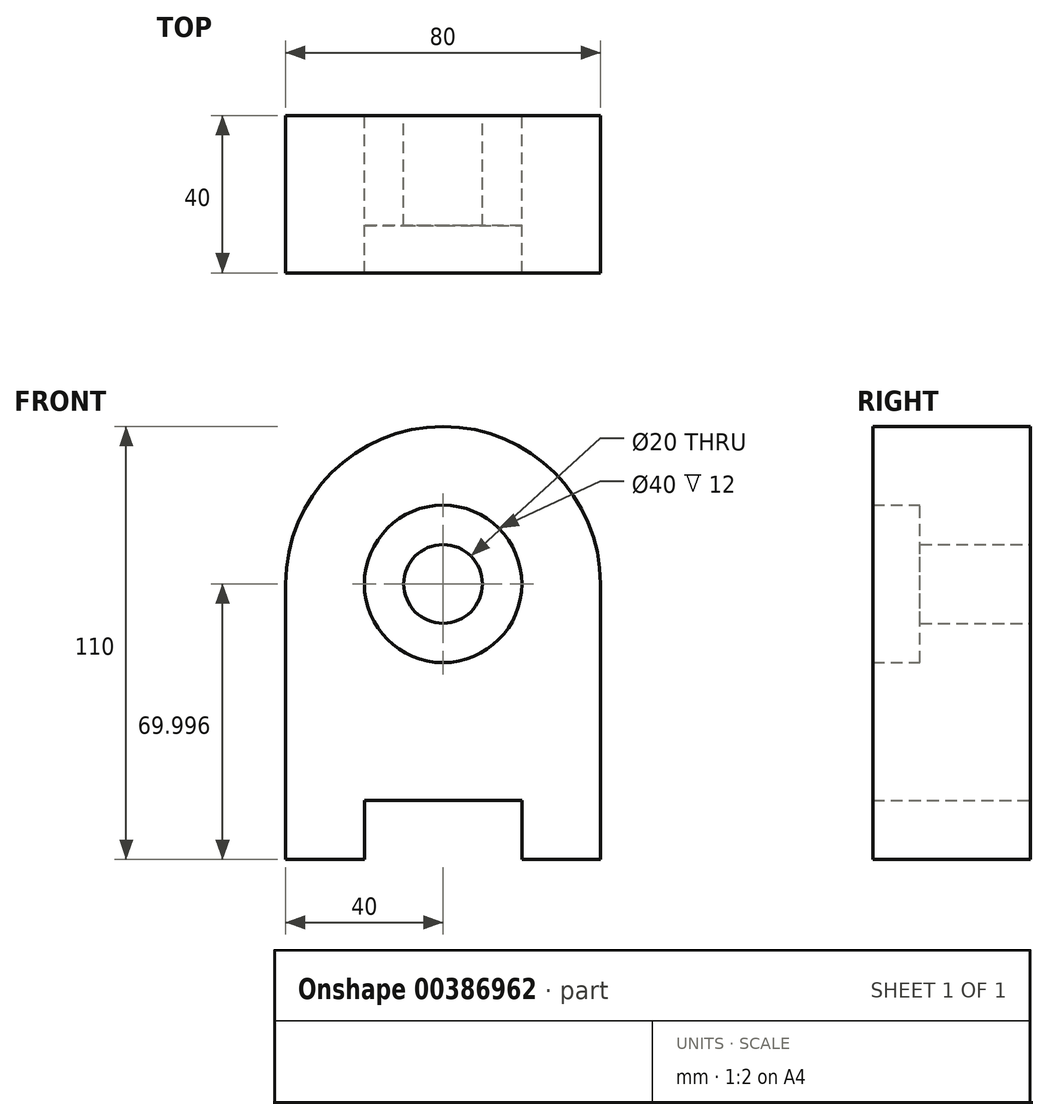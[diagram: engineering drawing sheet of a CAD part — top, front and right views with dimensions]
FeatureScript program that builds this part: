
annotation { "Feature Type Name" : "Feature", "Feature Type Description" : "" }
export const myFeature = defineFeature(function(context is Context, id is Id, definition is map)
    precondition{}
    {
        {
            var Q0;
            Q0=qCreatedBy(makeId("Front.planeOp"),FACE);
            var sketch = newSketch(context, id + "F0", { "sketchPlane" : qUnion([Q0])});
            skLineSegment(sketch, "E0.left", {"start": v(-40, 36.78) * mm, "end": v(-40, -33.22) * mm});
            skLineSegment(sketch, "E0.right", {"start": v(40, 36.78) * mm, "end": v(40, -33.22) * mm});
            skArc(sketch, "E1", {"start": v(40, 36.78) * mm, "mid": v(0, 76.78) * mm, "end": v(-40, 36.78) * mm});
            skCircle(sketch, "E2", {"center": v(0, 36.78) * mm, "radius": 20 * mm});
            skCircle(sketch, "E3", {"center": v(0, 36.78) * mm, "radius": 10 * mm});
            skLineSegment(sketch, "E4.left", {"start": v(-20, -18.22) * mm, "end": v(-20, -33.22) * mm});
            skLineSegment(sketch, "E4.right", {"start": v(20, -18.22) * mm, "end": v(20, -33.22) * mm});
            skLineSegment(sketch, "E5.trimOffspring", {"start": v(20, -33.22) * mm, "end": v(40, -33.22) * mm});
            skLineSegment(sketch, "E6", {"start": v(-40, -33.22) * mm, "end": v(-20, -33.22) * mm});
            skLineSegment(sketch, "E7.top", {"start": v(-40, -3.22) * mm, "end": v(40, -3.22) * mm});
            skLineSegment(sketch, "E8", {"start": v(-20, -18.22) * mm, "end": v(20, -18.22) * mm});
            skSolve(sketch);
        }
        {
            var Q0;
            Q0=makeQuery(id+"F0.imprint","IMPRINT",FACE,{"disambiguationData":[TD([[makeQuery(id+"F0.imprint","IMPRINT",EDGE,{"derivedFrom":sQuery(id+"F0.wireOp",EDGE,"E2")}),1.0]])]});
            extrude(context, id + "F1", {"entities" : qUnion([Q0]), "depth" : 28 * mm});
        }
        {
            var Q0;
            {var subQ0=sQuery(id+"F0.wireOp",EDGE,"E1");Q0=makeQuery(id+"F0.imprint","IMPRINT",FACE,{"disambiguationData":[TD([[makeQuery(id+"F0.imprint","IMPRINT",EDGE,{"derivedFrom":subQ0}),1.0]])]});}
            extrude(context, id + "F2", {"entities" : qUnion([Q0]), "operationType" : NewBodyOperationType.ADD, "depth" : 12 * mm});
        }
        {
            var Q0;
            Q0=makeQuery(id+"F0.imprint","IMPRINT",FACE,{"disambiguationData":[TD([[makeQuery(id+"F0.imprint","IMPRINT",EDGE,{"derivedFrom":sQuery(id+"F0.wireOp",EDGE,"E4.left")}),-1.0]])]});
            extrude(context, id + "F3", {"entities" : qUnion([Q0]), "operationType" : NewBodyOperationType.ADD, "depth" : 40 * mm});
        }
    });
